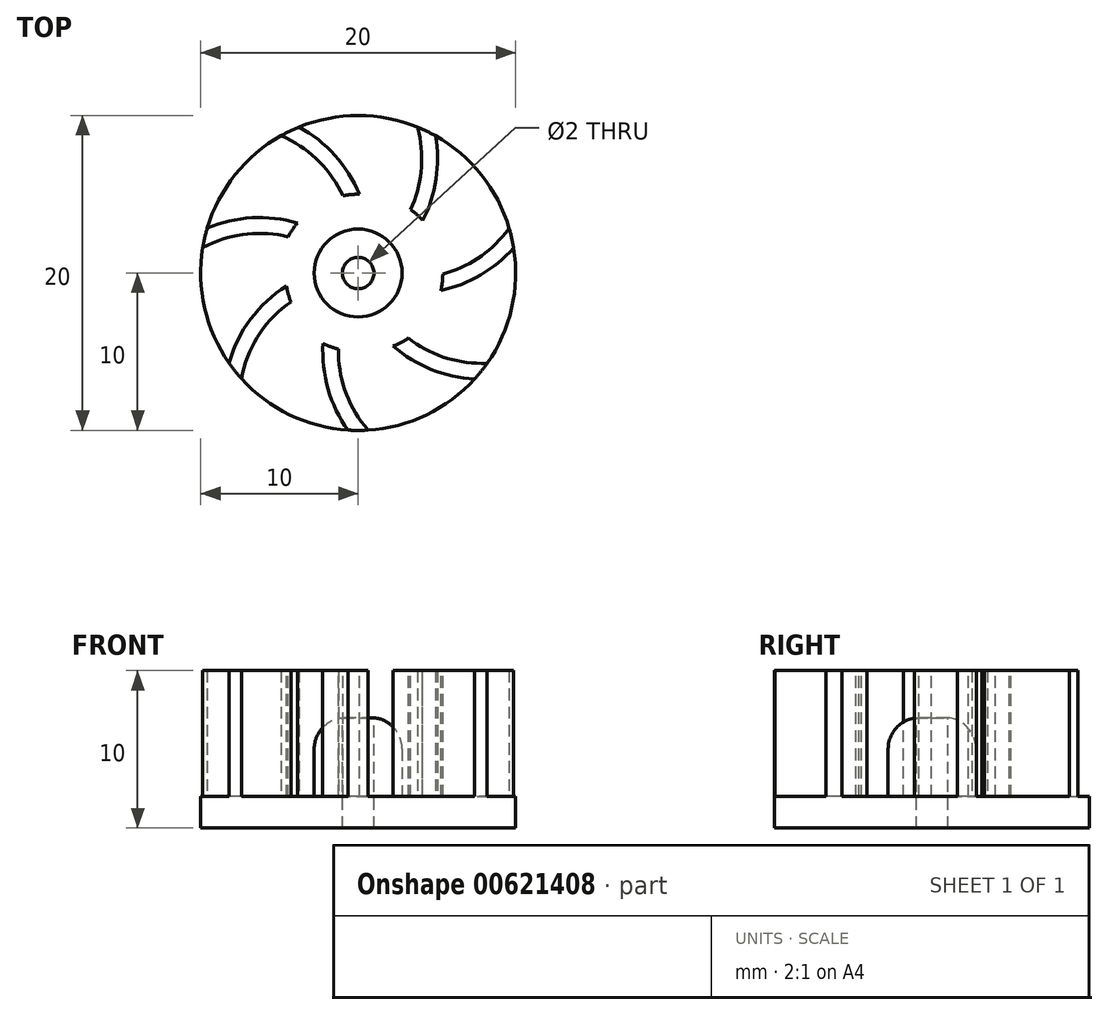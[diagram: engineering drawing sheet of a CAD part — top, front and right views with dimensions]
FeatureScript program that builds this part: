
annotation { "Feature Type Name" : "Feature", "Feature Type Description" : "" }
export const myFeature = defineFeature(function(context is Context, id is Id, definition is map)
    precondition{}
    {
        {
            var Q0;
            Q0=qCreatedBy(makeId("Top.planeOp"),FACE);
            var sketch = newSketch(context, id + "F0", { "sketchPlane" : qUnion([Q0])});
            skCircle(sketch, "E0", {"center": v(0, 0) * mm, "radius": 10 * mm});
            skSolve(sketch);
        }
        {
            var Q0;
            Q0=makeQuery(id+"F0.imprint","IMPRINT",FACE,{"disambiguationData":[TD([[makeQuery(id+"F0.imprint","IMPRINT",EDGE,{"derivedFrom":sQuery(id+"F0.wireOp",EDGE,"E0")}),1.0]])]});
            extrude(context, id + "F1", {"entities" : qUnion([Q0]), "depth" : 2 * mm, "offsetDistance" : 25 * mm});
        }
        {
            var Q0;
            Q0=makeQuery(id+"F1.opExtrude","CAP_FACE",FACE,{"disambiguationData":[OSD([sQuery(id+"F0.wireOp",EDGE,"E0")])],"isStart":false});
            var sketch = newSketch(context, id + "F2", { "sketchPlane" : qUnion([Q0])});
            skCircle(sketch, "E1", {"center": v(0, 0) * mm, "radius": 2.5 * mm});
            skPoint(sketch, "E2.end.orphan", {"position": v(0, -10) * mm});
            skArc(sketch, "E3.0", {"start": v(-0.78, -2.38) * mm, "mid": v(-1.16, -6.19) * mm, "end": v(0.4, -9.69) * mm});
            skArc(sketch, "E4.trimOffspring", {"start": v(-1.66, -1.87) * mm, "mid": v(-2.16, -6.26) * mm, "end": v(-0.4, -10.31) * mm});
            skPoint(sketch, "E5.start.orphan", {"position": v(-2.5, 0) * mm});
            skLineSegment(sketch, "E6", {"start": v(0.4, -9.69) * mm, "end": v(0.62, -9.98) * mm});
            skArc(sketch, "E7.1.0", {"start": v(0.43, -2.46) * mm, "mid": v(3.55, -5.59) * mm, "end": v(7.82, -6.73) * mm});
            skArc(sketch, "E7.1.1", {"start": v(1.37, -2.09) * mm, "mid": v(4.12, -4.76) * mm, "end": v(7.82, -5.73) * mm});
            skArc(sketch, "E7.2.0", {"start": v(2.2, -1.2) * mm, "mid": v(6.58, -0.7) * mm, "end": v(10.14, 1.91) * mm});
            skArc(sketch, "E7.2.1", {"start": v(2.49, -0.23) * mm, "mid": v(6.29, 0.25) * mm, "end": v(9.36, 2.54) * mm});
            skArc(sketch, "E7.3.0", {"start": v(2.3, 0.97) * mm, "mid": v(4.66, 4.7) * mm, "end": v(4.83, 9.12) * mm});
            skArc(sketch, "E7.3.1", {"start": v(1.73, 1.8) * mm, "mid": v(3.72, 5.07) * mm, "end": v(3.85, 8.9) * mm});
            skArc(sketch, "E7.4.0", {"start": v(0.68, 2.4) * mm, "mid": v(-0.78, 6.58) * mm, "end": v(-4.12, 9.46) * mm});
            skArc(sketch, "E7.4.1", {"start": v(-0.33, 2.48) * mm, "mid": v(-1.64, 6.07) * mm, "end": v(-4.56, 8.56) * mm});
            skArc(sketch, "E7.5.0", {"start": v(-1.46, 2.03) * mm, "mid": v(-5.63, 3.5) * mm, "end": v(-9.97, 2.68) * mm});
            skArc(sketch, "E7.5.1", {"start": v(-2.14, 1.29) * mm, "mid": v(-5.77, 2.5) * mm, "end": v(-9.53, 1.77) * mm});
            skArc(sketch, "E7.6.0", {"start": v(-2.5, 0.13) * mm, "mid": v(-6.24, -2.22) * mm, "end": v(-8.3, -6.12) * mm});
            skArc(sketch, "E7.6.1", {"start": v(-2.34, -0.87) * mm, "mid": v(-5.56, -2.95) * mm, "end": v(-7.33, -6.35) * mm});
            skLineSegment(sketch, "E8.1.0", {"start": v(7.82, -5.73) * mm, "end": v(8.2, -5.73) * mm});
            skLineSegment(sketch, "E8.2.0", {"start": v(9.36, 2.54) * mm, "end": v(9.6, 2.83) * mm});
            skLineSegment(sketch, "E8.3.0", {"start": v(3.85, 8.9) * mm, "end": v(3.77, 9.26) * mm});
            skLineSegment(sketch, "E8.4.0", {"start": v(-4.56, 8.56) * mm, "end": v(-4.9, 8.72) * mm});
            skLineSegment(sketch, "E8.5.0", {"start": v(-9.53, 1.77) * mm, "end": v(-9.87, 1.61) * mm});
            skLineSegment(sketch, "E8.6.0", {"start": v(-7.33, -6.35) * mm, "end": v(-7.41, -6.71) * mm});
            skSolve(sketch);
        }
        {
            var Q0;
            {var subQ1=sQuery(id+"F2.wireOp",EDGE,"E7.5.1");Q0=makeQuery(id+"F2.imprint","IMPRINT",FACE,{"disambiguationData":[TD([[makeQuery(id+"F2.imprint","IMPRINT",EDGE,{"derivedFrom":subQ1}),-1.0]])]});}
            var Q1;
            {var subQ0=sQuery(id+"F2.wireOp",EDGE,"E7.4.1");Q1=makeQuery(id+"F2.imprint","IMPRINT",FACE,{"disambiguationData":[TD([[makeQuery(id+"F2.imprint","IMPRINT",EDGE,{"derivedFrom":subQ0}),-1.0]])]});}
            var Q2;
            {var subQ0=sQuery(id+"F2.wireOp",EDGE,"E7.3.1");Q2=makeQuery(id+"F2.imprint","IMPRINT",FACE,{"disambiguationData":[TD([[makeQuery(id+"F2.imprint","IMPRINT",EDGE,{"derivedFrom":subQ0}),-1.0]])]});}
            var Q3;
            {var subQ6=sQuery(id+"F2.wireOp",EDGE,"E7.2.1");Q3=makeQuery(id+"F2.imprint","IMPRINT",FACE,{"disambiguationData":[TD([[makeQuery(id+"F2.imprint","IMPRINT",EDGE,{"derivedFrom":subQ6}),-1.0]])]});}
            var Q4;
            {var subQ1=sQuery(id+"F2.wireOp",EDGE,"E7.1.1");Q4=makeQuery(id+"F2.imprint","IMPRINT",FACE,{"disambiguationData":[TD([[makeQuery(id+"F2.imprint","IMPRINT",EDGE,{"derivedFrom":subQ1}),-1.0]])]});}
            var Q5;
            {var subQ6=sQuery(id+"F2.wireOp",EDGE,"E3.0");Q5=makeQuery(id+"F2.imprint","IMPRINT",FACE,{"disambiguationData":[TD([[makeQuery(id+"F2.imprint","IMPRINT",EDGE,{"derivedFrom":subQ6}),-1.0]])]});}
            var Q6;
            {var subQ1=sQuery(id+"F2.wireOp",EDGE,"E7.6.1");Q6=makeQuery(id+"F2.imprint","IMPRINT",FACE,{"disambiguationData":[TD([[makeQuery(id+"F2.imprint","IMPRINT",EDGE,{"derivedFrom":subQ1}),-1.0]])]});}
            extrude(context, id + "F3", {"entities" : qUnion([Q0, Q1, Q2, Q3, Q4, Q5, Q6]), "operationType" : NewBodyOperationType.ADD, "depth" : 8 * mm, "offsetDistance" : 25 * mm});
        }
        {
            var Q0;
            Q0=makeQuery(id+"F3.opExtrude","CAP_FACE",FACE,{"disambiguationData":[OSD([sQuery(id+"F0.wireOp",EDGE,"E0"),sQuery(id+"F2.wireOp",EDGE,"E1"),sQuery(id+"F2.wireOp",EDGE,"E7.6.0"),sQuery(id+"F2.wireOp",EDGE,"E7.6.1"),sQuery(id+"F2.wireOp",EDGE,"E8.6.0")])],"isStart":false});
            var sketch = newSketch(context, id + "F4", { "sketchPlane" : qUnion([Q0])});
            skCircle(sketch, "E9", {"center": v(0.25, 0) * mm, "radius": 5 * mm});
            skSolve(sketch);
        }
        {
            var Q0;
            {var subQ1=sQuery(id+"F2.wireOp",EDGE,"E7.6.0");var subQ7=sQuery(id+"F2.wireOp",EDGE,"E1");var subQ8=makeQuery(id+"F3.opExtrude","CAP_EDGE",EDGE,{"disambiguationData":[OSD([subQ7]),TDD([makeQuery(id+"F2.imprint","IMPRINT",EDGE,{"disambiguationData":[TD([[makeQuery(id+"F2.imprint","INTERSECT",VERTEX,{"derivedFrom":[subQ7,subQ1]}),-1.0]])],"derivedFrom":subQ7})])],"isStart":false});Q0=makeQuery(id+"F4.imprint","IMPRINT",FACE,{"disambiguationData":[TD([[makeQuery(id+"F4.imprint","IMPRINT",EDGE,{"derivedFrom":subQ8}),1.0]])]});}
            extrude(context, id + "F5", {"entities" : qUnion([Q0]), "operationType" : NewBodyOperationType.REMOVE, "oppositeDirection" : true, "depth" : 8 * mm, "offsetDistance" : 25 * mm});
        }
        {
            var Q0;
            Q0=makeQuery(id+"F3.opExtrude","CAP_FACE",FACE,{"disambiguationData":[OSD([sQuery(id+"F0.wireOp",EDGE,"E0"),sQuery(id+"F2.wireOp",EDGE,"E1"),sQuery(id+"F2.wireOp",EDGE,"E7.6.0"),sQuery(id+"F2.wireOp",EDGE,"E7.6.1"),sQuery(id+"F2.wireOp",EDGE,"E8.6.0")])],"isStart":false});
            var sketch = newSketch(context, id + "F6", { "sketchPlane" : qUnion([Q0])});
            skCircle(sketch, "E10", {"center": v(0, 0) * mm, "radius": 5 * mm});
            skSolve(sketch);
        }
        {
            var Q0;
            {var subQ1=sQuery(id+"F2.wireOp",EDGE,"E7.6.0");var subQ7=sQuery(id+"F2.wireOp",EDGE,"E1");var subQ8=makeQuery(id+"F3.opExtrude","CAP_EDGE",EDGE,{"disambiguationData":[OSD([subQ7]),TDD([makeQuery(id+"F2.imprint","IMPRINT",EDGE,{"disambiguationData":[TD([[makeQuery(id+"F2.imprint","INTERSECT",VERTEX,{"derivedFrom":[subQ7,subQ1]}),-1.0]])],"derivedFrom":subQ7})])],"isStart":false});Q0=makeQuery(id+"F6.imprint","IMPRINT",FACE,{"disambiguationData":[TD([[makeQuery(id+"F6.imprint","IMPRINT",EDGE,{"derivedFrom":subQ8}),1.0]])]});}
            extrude(context, id + "F7", {"entities" : qUnion([Q0]), "operationType" : NewBodyOperationType.REMOVE, "oppositeDirection" : true, "depth" : 8 * mm, "offsetDistance" : 25 * mm});
        }
        {
            var Q0;
            Q0=makeQuery(id+"F3.opExtrude","CAP_FACE",FACE,{"disambiguationData":[OSD([sQuery(id+"F0.wireOp",EDGE,"E0"),sQuery(id+"F2.wireOp",EDGE,"E1"),sQuery(id+"F2.wireOp",EDGE,"E7.4.0"),sQuery(id+"F2.wireOp",EDGE,"E7.4.1"),sQuery(id+"F2.wireOp",EDGE,"E8.4.0")])],"isStart":false});
            var sketch = newSketch(context, id + "F8", { "sketchPlane" : qUnion([Q0])});
            skCircle(sketch, "E11", {"center": v(0.38, 0) * mm, "radius": 5 * mm});
            skSolve(sketch);
        }
        {
            var Q0;
            Q0=makeQuery(id+"F8.imprint","IMPRINT",FACE,{"disambiguationData":[TD([[makeQuery(id+"F8.imprint","IMPRINT",EDGE,{"derivedFrom":sQuery(id+"F8.wireOp",EDGE,"E11")}),1.0]])]});
            extrude(context, id + "F9", {"entities" : qUnion([Q0]), "operationType" : NewBodyOperationType.REMOVE, "oppositeDirection" : true, "depth" : 8 * mm, "offsetDistance" : 25 * mm});
        }
        {
            var Q0;
            {var subQ0=sQuery(id+"F2.wireOp",EDGE,"E7.6.1");var subQ1=sQuery(id+"F2.wireOp",EDGE,"E7.6.0");var subQ2=sQuery(id+"F2.wireOp",EDGE,"E1");Q0=makeQuery(id+"F9.boolean.opBoolean","MERGE",FACE,{"derivedFrom":[makeQuery(id+"F7.boolean.opBoolean","MERGE",FACE,{"derivedFrom":[makeQuery(id+"F5.boolean.opBoolean","MERGE",FACE,{"derivedFrom":[makeQuery(id+"F1.opExtrude","CAP_FACE",FACE,{"disambiguationData":[OSD([sQuery(id+"F0.wireOp",EDGE,"E0")])],"isStart":false}),makeQuery(id+"F5.opExtrude","CAP_FACE",FACE,{"disambiguationData":[OSD([subQ2,subQ1,subQ0,sQuery(id+"F4.wireOp",EDGE,"E9")])],"isStart":false})]}),makeQuery(id+"F7.opExtrude","CAP_FACE",FACE,{"disambiguationData":[OSD([subQ2,subQ1,subQ0,sQuery(id+"F6.wireOp",EDGE,"E10")])],"isStart":false})]}),makeQuery(id+"F9.opExtrude","CAP_FACE",FACE,{"disambiguationData":[OSD([sQuery(id+"F8.wireOp",EDGE,"E11")])],"isStart":false})]});}
            var sketch = newSketch(context, id + "F10", { "sketchPlane" : qUnion([Q0])});
            skCircle(sketch, "E12", {"center": v(0, 0) * mm, "radius": 2.8 * mm});
            skSolve(sketch);
        }
        {
            var Q0;
            Q0=makeQuery(id+"F10.imprint","IMPRINT",FACE,{"disambiguationData":[TD([[makeQuery(id+"F10.imprint","IMPRINT",EDGE,{"derivedFrom":sQuery(id+"F10.wireOp",EDGE,"E12")}),1.0]])]});
            extrude(context, id + "F11", {"entities" : qUnion([Q0]), "operationType" : NewBodyOperationType.ADD, "depth" : 5 * mm, "offsetDistance" : 25 * mm});
        }
        {
            var Q0;
            Q0=makeQuery(id+"F11.opExtrude","CAP_FACE",FACE,{"disambiguationData":[OSD([sQuery(id+"F10.wireOp",EDGE,"E12")])],"isStart":false});
            var sketch = newSketch(context, id + "F12", { "sketchPlane" : qUnion([Q0])});
            skCircle(sketch, "E13", {"center": v(0, 0) * mm, "radius": 1 * mm});
            skSolve(sketch);
        }
        {
            var Q0;
            Q0 = qSketchRegion(id + "F12", true);
            extrude(context, id + "F13", {"entities" : qUnion([Q0]), "operationType" : NewBodyOperationType.REMOVE, "oppositeDirection" : true, "depth" : 25 * mm, "offsetDistance" : 25 * mm});
        }
        {
            var Q0;
            Q0=makeQuery(id+"F11.opExtrude","CAP_EDGE",EDGE,{"disambiguationData":[OSD([sQuery(id+"F10.wireOp",EDGE,"E12")])],"isStart":false});
            fillet(context, id + "F14", {"entities" : qUnion([Q0]), "radius" : 2 * mm, "tangentPropagation" : true, "allowEdgeOverflow" : false});
        }
    });
